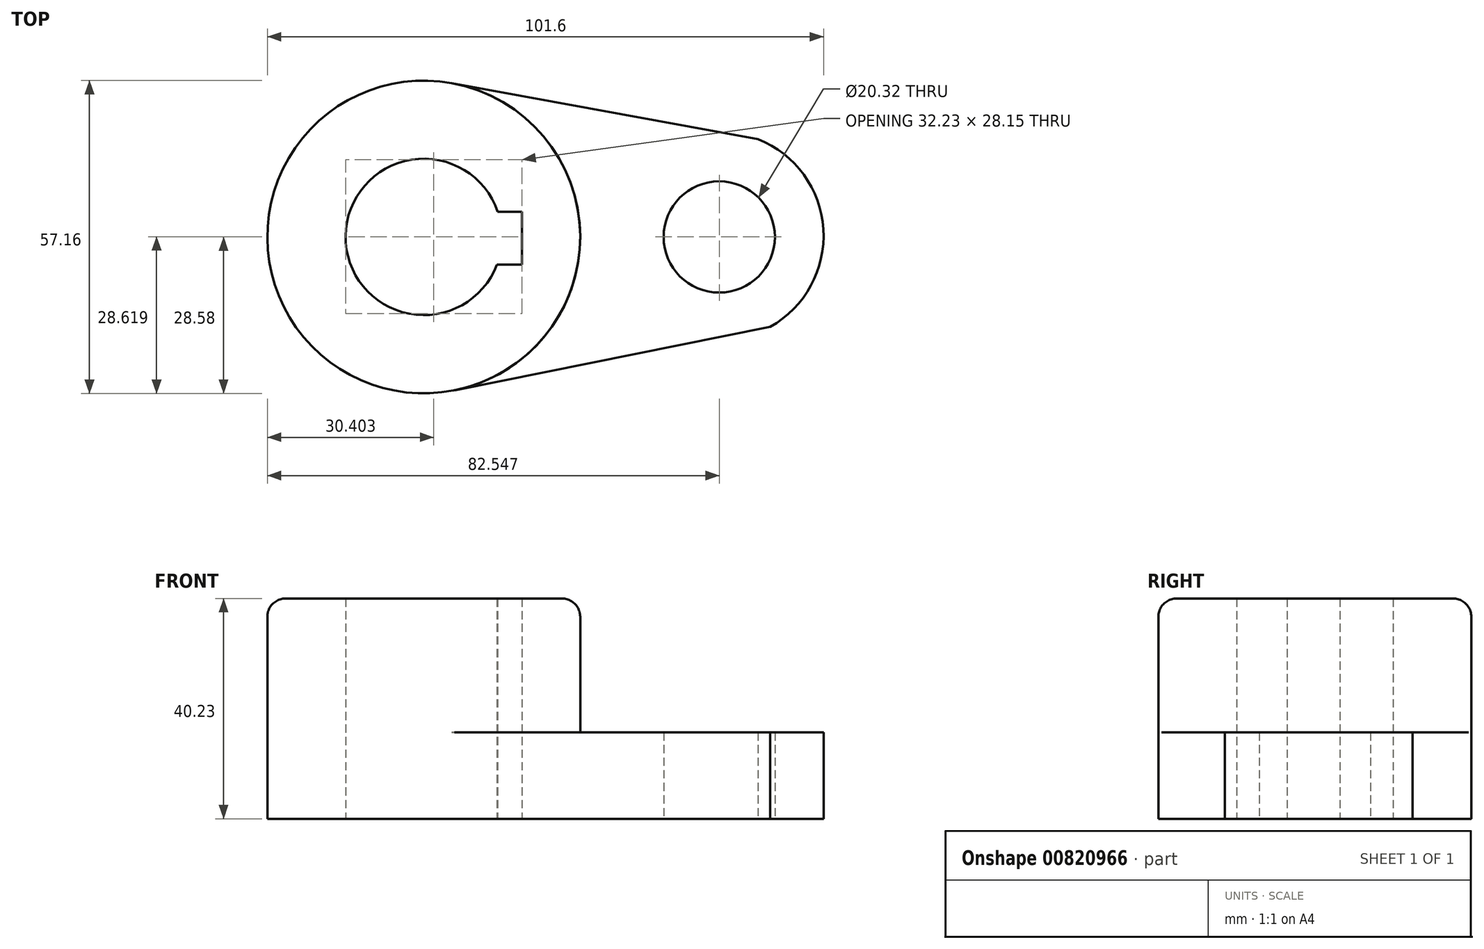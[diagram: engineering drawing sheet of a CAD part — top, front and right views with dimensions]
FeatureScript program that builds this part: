
annotation { "Feature Type Name" : "Feature", "Feature Type Description" : "" }
export const myFeature = defineFeature(function(context is Context, id is Id, definition is map)
    precondition{}
    {
        {
            var Q0;
            Q0=qCreatedBy(makeId("Top.planeOp"),FACE);
            var sketch = newSketch(context, id + "F0", { "sketchPlane" : qUnion([Q0])});
            skCircle(sketch, "E0", {"center": v(-50.56, 0) * mm, "radius": 28.58 * mm});
            skArc(sketch, "E1", {"start": v(-37.03, 4.61) * mm, "mid": v(-64.84, 0.23) * mm, "end": v(-37.19, -5.04) * mm});
            skCircle(sketch, "E2", {"center": v(3.42, 0) * mm, "radius": 10.16 * mm});
            skLineSegment(sketch, "E3", {"start": v(-45.42, 28.1) * mm, "end": v(10.52, 17.88) * mm});
            skLineSegment(sketch, "E4", {"start": v(-44.92, -28.01) * mm, "end": v(12.73, -16.41) * mm});
            skArc(sketch, "E5", {"start": v(12.73, -16.41) * mm, "mid": v(22.43, 1.43) * mm, "end": v(10.52, 17.88) * mm});
            skLineSegment(sketch, "E6", {"start": v(-37.03, 4.61) * mm, "end": v(-32.61, 4.61) * mm});
            skLineSegment(sketch, "E7", {"start": v(-32.61, 4.61) * mm, "end": v(-32.61, -5.04) * mm});
            skLineSegment(sketch, "E8", {"start": v(-32.61, -5.04) * mm, "end": v(-37.19, -5.04) * mm});
            skSolve(sketch);
        }
        {
            var Q0;
            Q0=makeQuery(id+"F0.imprint","IMPRINT",FACE,{"disambiguationData":[TD([[makeQuery(id+"F0.imprint","IMPRINT",EDGE,{"derivedFrom":sQuery(id+"F0.wireOp",EDGE,"E1")}),-1.0]])]});
            extrude(context, id + "F1", {"entities" : qUnion([Q0]), "depth" : 40.23 * mm, "offsetDistance" : 25.4 * mm});
        }
        {
            var Q0;
            Q0=makeQuery(id+"F0.imprint","IMPRINT",FACE,{"disambiguationData":[TD([[makeQuery(id+"F0.imprint","IMPRINT",EDGE,{"derivedFrom":sQuery(id+"F0.wireOp",EDGE,"E2")}),-1.0]])]});
            extrude(context, id + "F2", {"entities" : qUnion([Q0]), "operationType" : NewBodyOperationType.ADD, "depth" : 15.77 * mm, "offsetDistance" : 25.4 * mm});
        }
        {
            var Q0;
            Q0=makeQuery(id+"F1.opExtrude","CAP_EDGE",EDGE,{"disambiguationData":[OSD([sQuery(id+"F0.wireOp",EDGE,"E0")])],"isStart":false});
            fillet(context, id + "F3", {"entities" : qUnion([Q0]), "radius" : 3.3 * mm, "tangentPropagation" : true, "allowEdgeOverflow" : false});
        }
    });
